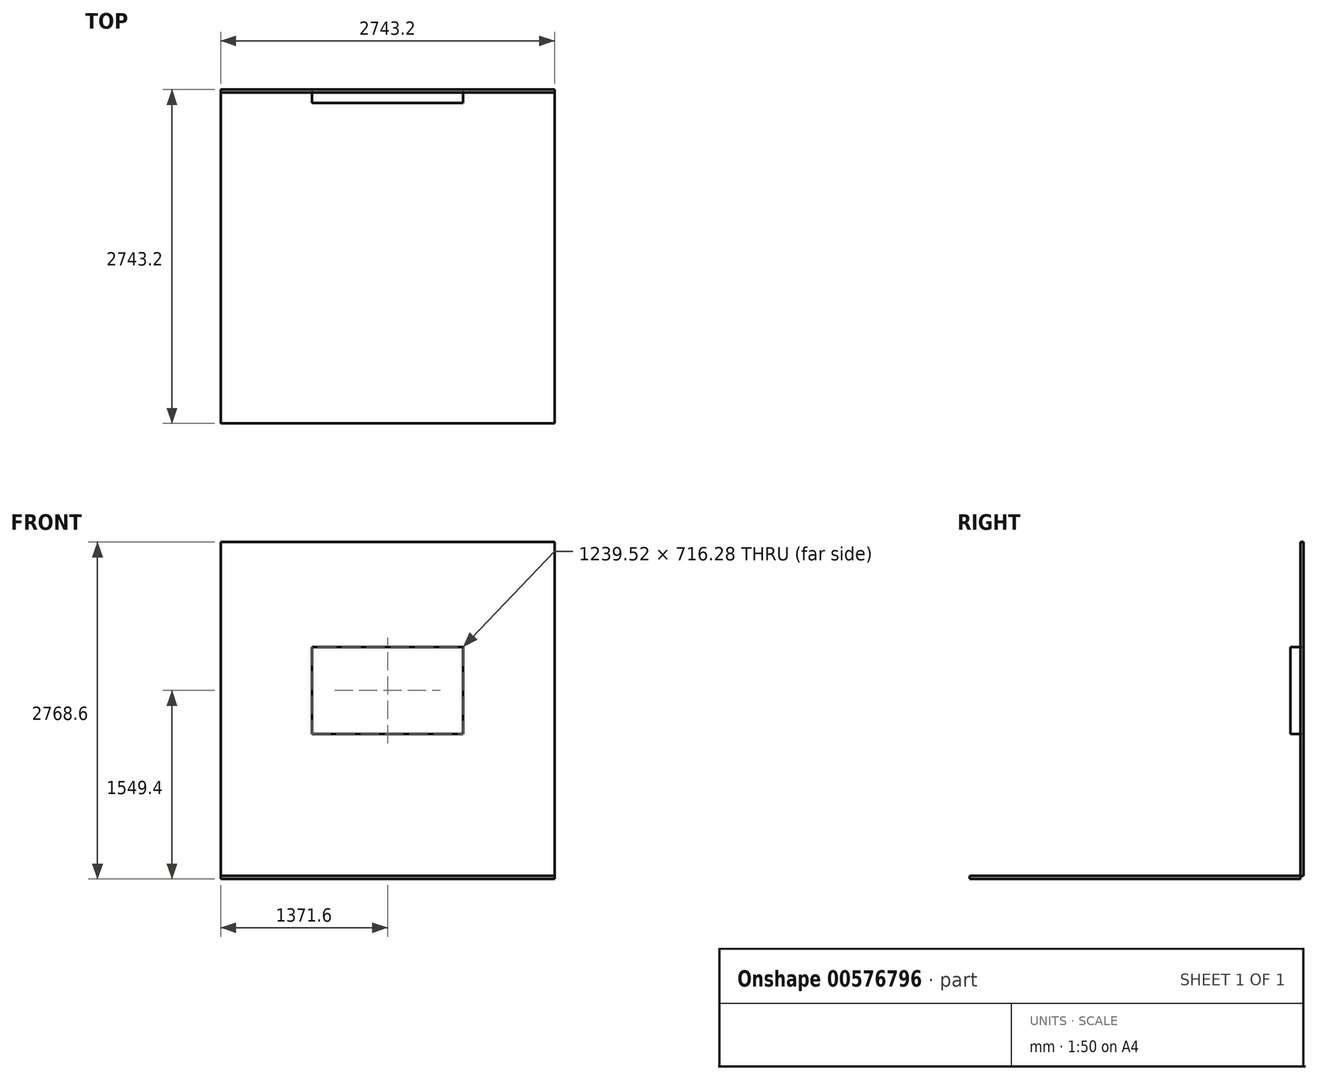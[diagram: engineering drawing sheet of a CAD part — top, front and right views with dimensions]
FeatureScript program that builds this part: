
annotation { "Feature Type Name" : "Feature", "Feature Type Description" : "" }
export const myFeature = defineFeature(function(context is Context, id is Id, definition is map)
    precondition{}
    {
        {
            var Q0;
            Q0=qCreatedBy(makeId("Front.planeOp"),FACE);
            var sketch = newSketch(context, id + "F0", { "sketchPlane" : qUnion([Q0])});
            skLineSegment(sketch, "E0.bottom", {"start": v(-619.76, 358.14) * mm, "end": v(619.76, 358.14) * mm});
            skLineSegment(sketch, "E0.top", {"start": v(-619.76, -358.14) * mm, "end": v(619.76, -358.14) * mm});
            skLineSegment(sketch, "E0.left", {"start": v(-619.76, 358.14) * mm, "end": v(-619.76, -358.14) * mm});
            skLineSegment(sketch, "E0.right", {"start": v(619.76, 358.14) * mm, "end": v(619.76, -358.14) * mm});
            skSolve(sketch);
        }
        {
            var Q0;
            Q0=makeQuery(id+"F0.imprint","IMPRINT",FACE,{"disambiguationData":[TD([[makeQuery(id+"F0.imprint","IMPRINT",EDGE,{"derivedFrom":sQuery(id+"F0.wireOp",EDGE,"E0.bottom")}),-1.0]])]});
            extrude(context, id + "F1", {"entities" : qUnion([Q0]), "depth" : 83.82 * mm, "offsetDistance" : 25.4 * mm});
        }
        {
            var Q0;
            Q0=makeQuery(id+"F1.opExtrude","CAP_FACE",FACE,{"disambiguationData":[OSD([sQuery(id+"F0.wireOp",EDGE,"E0.bottom"),sQuery(id+"F0.wireOp",EDGE,"E0.top"),sQuery(id+"F0.wireOp",EDGE,"E0.left"),sQuery(id+"F0.wireOp",EDGE,"E0.right")])],"isStart":true});
            var sketch = newSketch(context, id + "F2", { "sketchPlane" : qUnion([Q0])});
            skLineSegment(sketch, "E1.bottom", {"start": v(-1371.6, -1524) * mm, "end": v(1371.6, -1524) * mm});
            skLineSegment(sketch, "E1.top", {"start": v(-1371.6, 1219.2) * mm, "end": v(1371.6, 1219.2) * mm});
            skLineSegment(sketch, "E1.left", {"start": v(-1371.6, -1524) * mm, "end": v(-1371.6, 1219.2) * mm});
            skLineSegment(sketch, "E1.right", {"start": v(1371.6, -1524) * mm, "end": v(1371.6, 1219.2) * mm});
            skSolve(sketch);
        }
        {
            var Q0;
            Q0=makeQuery(id+"F2.imprint","IMPRINT",FACE,{"disambiguationData":[TD([[makeQuery(id+"F2.imprint","IMPRINT",EDGE,{"derivedFrom":sQuery(id+"F2.wireOp",EDGE,"E1.bottom")}),1.0]])]});
            extrude(context, id + "F3", {"entities" : qUnion([Q0]), "depth" : 25.4 * mm, "offsetDistance" : 25.4 * mm});
        }
        {
            var Q0;
            Q0=makeQuery(id+"F3.opExtrude","SWEPT_FACE",FACE,{"disambiguationData":[OSD([sQuery(id+"F2.wireOp",EDGE,"E1.bottom")])]});
            var sketch = newSketch(context, id + "F4", { "sketchPlane" : qUnion([Q0])});
            skLineSegment(sketch, "E2.bottom", {"start": v(-1371.6, -25.4) * mm, "end": v(1371.6, -25.4) * mm});
            skLineSegment(sketch, "E2.top", {"start": v(-1371.6, 2717.8) * mm, "end": v(1371.6, 2717.8) * mm});
            skLineSegment(sketch, "E2.left", {"start": v(-1371.6, -25.4) * mm, "end": v(-1371.6, 2717.8) * mm});
            skLineSegment(sketch, "E2.right", {"start": v(1371.6, -25.4) * mm, "end": v(1371.6, 2717.8) * mm});
            skSolve(sketch);
        }
        {
            var Q0;
            {var subQ0=sQuery(id+"F4.wireOp",EDGE,"E2.top");Q0=makeQuery(id+"F4.imprint","IMPRINT",FACE,{"disambiguationData":[TD([[makeQuery(id+"F4.imprint","IMPRINT",EDGE,{"derivedFrom":subQ0}),-1.0]])]});}
            extrude(context, id + "F5", {"entities" : qUnion([Q0]), "depth" : 25.4 * mm, "offsetDistance" : 25.4 * mm});
        }
    });
